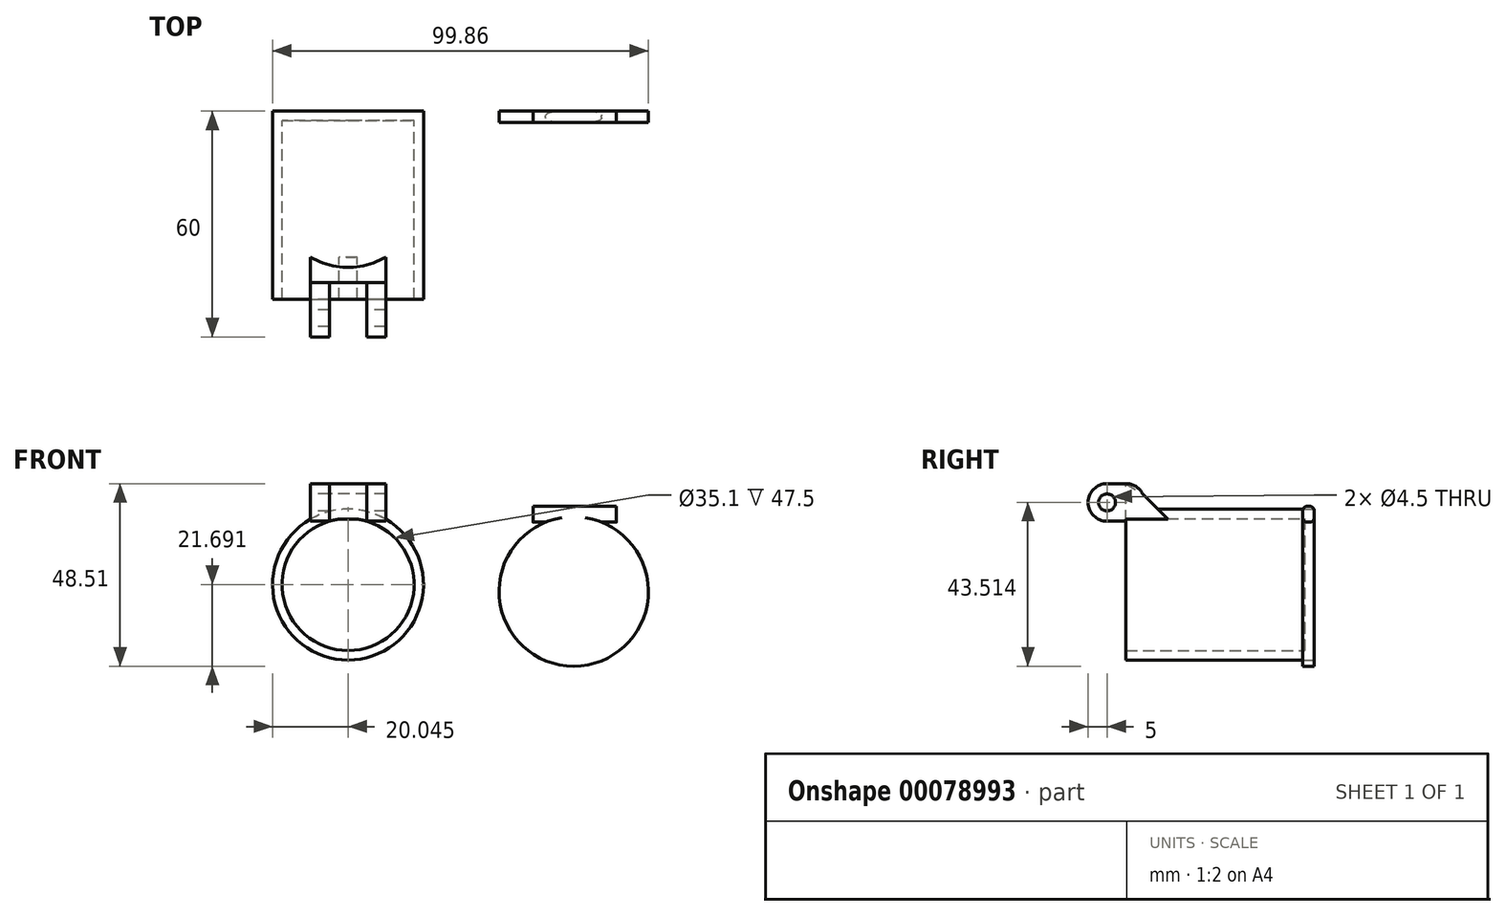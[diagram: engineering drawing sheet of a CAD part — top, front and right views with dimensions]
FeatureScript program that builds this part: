
annotation { "Feature Type Name" : "Feature", "Feature Type Description" : "" }
export const myFeature = defineFeature(function(context is Context, id is Id, definition is map)
    precondition{}
    {
        {
            var Q0;
            Q0=qCreatedBy(makeId("Front.planeOp"),FACE);
            var sketch = newSketch(context, id + "F0", { "sketchPlane" : qUnion([Q0])});
            skCircle(sketch, "E0", {"center": v(-20.43, 1.83) * mm, "radius": 20.05 * mm});
            skSolve(sketch);
        }
        {
            var Q0;
            Q0 = qSketchRegion(id + "F0", true);
            extrude(context, id + "F1", {"entities" : qUnion([Q0]), "depth" : 50 * mm});
        }
        {
            var Q0;
            Q0=makeQuery(id+"F1.opExtrude","CAP_FACE",FACE,{"disambiguationData":[OSD([sQuery(id+"F0.wireOp",EDGE,"E0")])],"isStart":false});
            shell(context, id + "F2", {"entities" : qUnion([Q0]), "thickness" : 2.5 * mm});
        }
        {
            var Q0;
            Q0=makeQuery(id+"F1.opExtrude","CAP_FACE",FACE,{"disambiguationData":[OSD([sQuery(id+"F0.wireOp",EDGE,"E0")])],"isStart":false});
            cPlane(context, id + "F3", {"entities" : qUnion([Q0]), "cplaneType" : CPlaneType.OFFSET, "offset" : 5 * mm, "oppositeDirection" : true, "width" : 150 * mm, "height" : 150 * mm});
        }
        {
            var Q0;
            Q0=qCreatedBy(id+"F3.planeOp",FACE);
            var sketch = newSketch(context, id + "F4", { "sketchPlane" : qUnion([Q0])});
            skLineSegment(sketch, "E1.bottom", {"start": v(-30.43, 28.65) * mm, "end": v(-25.43, 28.65) * mm});
            skLineSegment(sketch, "E1.top", {"start": v(-30.43, 18.65) * mm, "end": v(-25.43, 18.65) * mm});
            skLineSegment(sketch, "E1.left", {"start": v(-30.43, 28.65) * mm, "end": v(-30.43, 18.65) * mm});
            skLineSegment(sketch, "E1.right", {"start": v(-25.43, 28.65) * mm, "end": v(-25.43, 18.65) * mm});
            skLineSegment(sketch, "E2.bottom", {"start": v(-15.43, 18.65) * mm, "end": v(-10.43, 18.65) * mm});
            skLineSegment(sketch, "E2.top", {"start": v(-15.43, 28.65) * mm, "end": v(-10.43, 28.65) * mm});
            skLineSegment(sketch, "E2.left", {"start": v(-15.43, 18.65) * mm, "end": v(-15.43, 28.65) * mm});
            skLineSegment(sketch, "E2.right", {"start": v(-10.43, 18.65) * mm, "end": v(-10.43, 28.65) * mm});
            skLineSegment(sketch, "E3", {"start": v(-20.43, 1.83) * mm, "end": v(-20.43, 31.74) * mm, "construction": true});
            skSolve(sketch);
        }
        {
            var Q0;
            {var subQ0=sQuery(id+"F4.wireOp",EDGE,"E1.top");Q0=makeQuery(id+"F4.imprint","IMPRINT",FACE,{"disambiguationData":[TD([[makeQuery(id+"F4.imprint","IMPRINT",EDGE,{"derivedFrom":subQ0}),1.0]])]});}
            var Q1;
            {var subQ0=sQuery(id+"F4.wireOp",EDGE,"E1.bottom");Q1=makeQuery(id+"F4.imprint","IMPRINT",FACE,{"disambiguationData":[TD([[makeQuery(id+"F4.imprint","IMPRINT",EDGE,{"derivedFrom":subQ0}),-1.0]])]});}
            var Q2;
            {var subQ0=sQuery(id+"F4.wireOp",EDGE,"E2.bottom");Q2=makeQuery(id+"F4.imprint","IMPRINT",FACE,{"disambiguationData":[TD([[makeQuery(id+"F4.imprint","IMPRINT",EDGE,{"derivedFrom":subQ0}),1.0]])]});}
            var Q3;
            {var subQ0=sQuery(id+"F4.wireOp",EDGE,"E2.top");Q3=makeQuery(id+"F4.imprint","IMPRINT",FACE,{"disambiguationData":[TD([[makeQuery(id+"F4.imprint","IMPRINT",EDGE,{"derivedFrom":subQ0}),-1.0]])]});}
            extrude(context, id + "F5", {"entities" : qUnion([Q0, Q1, Q2, Q3]), "operationType" : NewBodyOperationType.ADD, "depth" : 15 * mm});
        }
        {
            var Q0;
            Q0=makeQuery(id+"F5.opExtrude","CAP_EDGE",EDGE,{"disambiguationData":[OSD([sQuery(id+"F4.wireOp",EDGE,"E2.top")])],"isStart":true});
            var Q1;
            Q1=makeQuery(id+"F5.opExtrude","CAP_EDGE",EDGE,{"disambiguationData":[OSD([sQuery(id+"F4.wireOp",EDGE,"E1.bottom")])],"isStart":true});
            var Q2;
            Q2=makeQuery(id+"F5.opExtrude","CAP_EDGE",EDGE,{"disambiguationData":[OSD([sQuery(id+"F4.wireOp",EDGE,"E1.top")])],"isStart":false});
            var Q3;
            Q3=makeQuery(id+"F5.opExtrude","CAP_EDGE",EDGE,{"disambiguationData":[OSD([sQuery(id+"F4.wireOp",EDGE,"E2.bottom")])],"isStart":false});
            var Q4;
            Q4=makeQuery(id+"F5.opExtrude","CAP_EDGE",EDGE,{"disambiguationData":[OSD([sQuery(id+"F4.wireOp",EDGE,"E2.top")])],"isStart":false});
            var Q5;
            Q5=makeQuery(id+"F5.opExtrude","CAP_EDGE",EDGE,{"disambiguationData":[OSD([sQuery(id+"F4.wireOp",EDGE,"E1.bottom")])],"isStart":false});
            fillet(context, id + "F6", {"entities" : qUnion([Q0, Q1, Q2, Q3, Q4, Q5]), "radius" : 5 * mm, "tangentPropagation" : true, "allowEdgeOverflow" : false});
        }
        {
            var Q0;
            Q0=makeQuery(id+"F5.opExtrude","SWEPT_FACE",FACE,{"disambiguationData":[OSD([sQuery(id+"F4.wireOp",EDGE,"E1.left")])]});
            var sketch = newSketch(context, id + "F7", { "sketchPlane" : qUnion([Q0])});
            skCircle(sketch, "E4", {"center": v(55, 23.65) * mm, "radius": 1.5 * mm});
            skSolve(sketch);
        }
        {
            var Q0;
            Q0=sQuery(id+"F7.wireOp",VERTEX,"E4.center");
            var Q1;
            Q1=makeQuery(id+"F1.opExtrude","SWEPT_BODY",BODY,{"disambiguationData":[OSD([sQuery(id+"F0.wireOp",EDGE,"E0")])]});
            hole(context, id + "F8", {"style" : HoleStyle.SIMPLE, "endStyle" : HoleEndStyle.THROUGH, "holeDiameter" : 4.5 * mm, "locations" : qUnion([Q0]), "scope" : qUnion([Q1]), "isTappedThrough" : true});
        }
        {
            var Q0;
            Q0=qCreatedBy(makeId("Front.planeOp"),FACE);
            var sketch = newSketch(context, id + "F9", { "sketchPlane" : qUnion([Q0])});
            skCircle(sketch, "E5", {"center": v(39.52, 0) * mm, "radius": 19.86 * mm});
            skLineSegment(sketch, "E6.bottom", {"start": v(28.72, 22.65) * mm, "end": v(50.9, 22.65) * mm});
            skLineSegment(sketch, "E6.top", {"start": v(28.72, 18.41) * mm, "end": v(50.9, 18.41) * mm});
            skLineSegment(sketch, "E6.left", {"start": v(28.72, 22.65) * mm, "end": v(28.72, 18.41) * mm});
            skLineSegment(sketch, "E6.right", {"start": v(50.9, 22.65) * mm, "end": v(50.9, 18.41) * mm});
            skSolve(sketch);
        }
        {
            var Q0;
            Q0=makeQuery(id+"F9.imprint","IMPRINT",FACE,{"disambiguationData":[TD([[makeQuery(id+"F9.imprint","IMPRINT",EDGE,{"derivedFrom":sQuery(id+"F9.wireOp",EDGE,"E6.bottom")}),-1.0]])]});
            var Q1;
            {var subQ0=sQuery(id+"F9.wireOp",EDGE,"E6.top");var subQ1=sQuery(id+"F9.wireOp",EDGE,"E5");var subQ2=makeQuery(id+"F9.imprint","INTERSECT",VERTEX,{"disambiguationData":[OD(0.0)],"derivedFrom":[subQ1,subQ0]});Q1=makeQuery(id+"F9.imprint","IMPRINT",FACE,{"disambiguationData":[TD([[makeQuery(id+"F9.imprint","IMPRINT",EDGE,{"disambiguationData":[TD([[subQ2,1.0]])],"derivedFrom":subQ1}),1.0]])]});}
            var Q2;
            {var subQ0=sQuery(id+"F9.wireOp",EDGE,"E6.top");var subQ1=sQuery(id+"F9.wireOp",EDGE,"E5");var subQ2=makeQuery(id+"F9.imprint","INTERSECT",VERTEX,{"disambiguationData":[OD(0.0)],"derivedFrom":[subQ1,subQ0]});Q2=makeQuery(id+"F9.imprint","IMPRINT",FACE,{"disambiguationData":[TD([[makeQuery(id+"F9.imprint","IMPRINT",EDGE,{"disambiguationData":[TD([[subQ2,-1.0]])],"derivedFrom":subQ1}),1.0]])]});}
            extrude(context, id + "F10", {"entities" : qUnion([Q0, Q1, Q2]), "depth" : 3 * mm});
        }
        {
            var Q0;
            Q0=makeQuery(id+"F10.opExtrude","CAP_EDGE",EDGE,{"disambiguationData":[OSD([sQuery(id+"F9.wireOp",EDGE,"E6.bottom")])],"isStart":true});
            var Q1;
            Q1=makeQuery(id+"F10.opExtrude","CAP_EDGE",EDGE,{"disambiguationData":[OSD([sQuery(id+"F9.wireOp",EDGE,"E6.bottom")])],"isStart":false});
            var Q2;
            {var subQ0=sQuery(id+"F9.wireOp",EDGE,"E6.top");Q2=makeQuery(id+"F10.opExtrude","CAP_EDGE",EDGE,{"disambiguationData":[OSD([subQ0]),TDD([makeQuery(id+"F9.imprint","IMPRINT",EDGE,{"disambiguationData":[TD([[makeQuery(id+"F9.imprint","INTERSECT",VERTEX,{"derivedFrom":[subQ0,sQuery(id+"F9.wireOp",EDGE,"E6.left")]}),-1.0]])],"derivedFrom":subQ0})])],"isStart":true});}
            var Q3;
            {var subQ0=sQuery(id+"F9.wireOp",EDGE,"E6.top");Q3=makeQuery(id+"F10.opExtrude","CAP_EDGE",EDGE,{"disambiguationData":[OSD([subQ0]),TDD([makeQuery(id+"F9.imprint","IMPRINT",EDGE,{"disambiguationData":[TD([[makeQuery(id+"F9.imprint","INTERSECT",VERTEX,{"derivedFrom":[subQ0,sQuery(id+"F9.wireOp",EDGE,"E6.right")]}),1.0]])],"derivedFrom":subQ0})])],"isStart":true});}
            var Q4;
            {var subQ0=sQuery(id+"F9.wireOp",EDGE,"E6.top");Q4=makeQuery(id+"F10.opExtrude","CAP_EDGE",EDGE,{"disambiguationData":[OSD([subQ0]),TDD([makeQuery(id+"F9.imprint","IMPRINT",EDGE,{"disambiguationData":[TD([[makeQuery(id+"F9.imprint","INTERSECT",VERTEX,{"derivedFrom":[subQ0,sQuery(id+"F9.wireOp",EDGE,"E6.right")]}),1.0]])],"derivedFrom":subQ0})])],"isStart":false});}
            var Q5;
            {var subQ0=sQuery(id+"F9.wireOp",EDGE,"E6.top");Q5=makeQuery(id+"F10.opExtrude","CAP_EDGE",EDGE,{"disambiguationData":[OSD([subQ0]),TDD([makeQuery(id+"F9.imprint","IMPRINT",EDGE,{"disambiguationData":[TD([[makeQuery(id+"F9.imprint","INTERSECT",VERTEX,{"derivedFrom":[subQ0,sQuery(id+"F9.wireOp",EDGE,"E6.left")]}),-1.0]])],"derivedFrom":subQ0})])],"isStart":false});}
            fillet(context, id + "F11", {"entities" : qUnion([Q0, Q1, Q2, Q3, Q4, Q5]), "radius" : 1.2 * mm, "tangentPropagation" : true, "allowEdgeOverflow" : false});
        }
        {
            var Q0;
            Q0=makeQuery(id+"F5.opExtrude","SWEPT_FACE",FACE,{"disambiguationData":[OSD([sQuery(id+"F4.wireOp",EDGE,"E1.left")])]});
            var sketch = newSketch(context, id + "F12", { "sketchPlane" : qUnion([Q0])});
            skLineSegment(sketch, "E7", {"start": v(45, 19.2) * mm, "end": v(38.83, 19.2) * mm});
            skLineSegment(sketch, "E8", {"start": v(38.83, 19.2) * mm, "end": v(45.54, 25.92) * mm});
            skLineSegment(sketch, "E9", {"start": v(45.54, 25.92) * mm, "end": v(45, 19.2) * mm});
            skLineSegment(sketch, "E10", {"start": v(45.54, 25.92) * mm, "end": v(50, 28.65) * mm});
            skLineSegment(sketch, "E11", {"start": v(50, 28.65) * mm, "end": v(50, 19.2) * mm});
            skLineSegment(sketch, "E12", {"start": v(50, 19.2) * mm, "end": v(45, 19.2) * mm});
            skSolve(sketch);
        }
        {
            var Q0;
            Q0 = qSketchRegion(id + "F12", true);
            var Q1;
            Q1=makeQuery(id+"F5.opExtrude","SWEPT_FACE",FACE,{"disambiguationData":[OSD([sQuery(id+"F4.wireOp",EDGE,"E2.right")])]});
            extrude(context, id + "F13", {"entities" : qUnion([Q0]), "operationType" : NewBodyOperationType.ADD, "endBound" : BoundingType.UP_TO_SURFACE, "oppositeDirection" : true, "endBoundEntityFace" : qUnion([Q1]), "depth" : 25 * mm});
        }
    });
